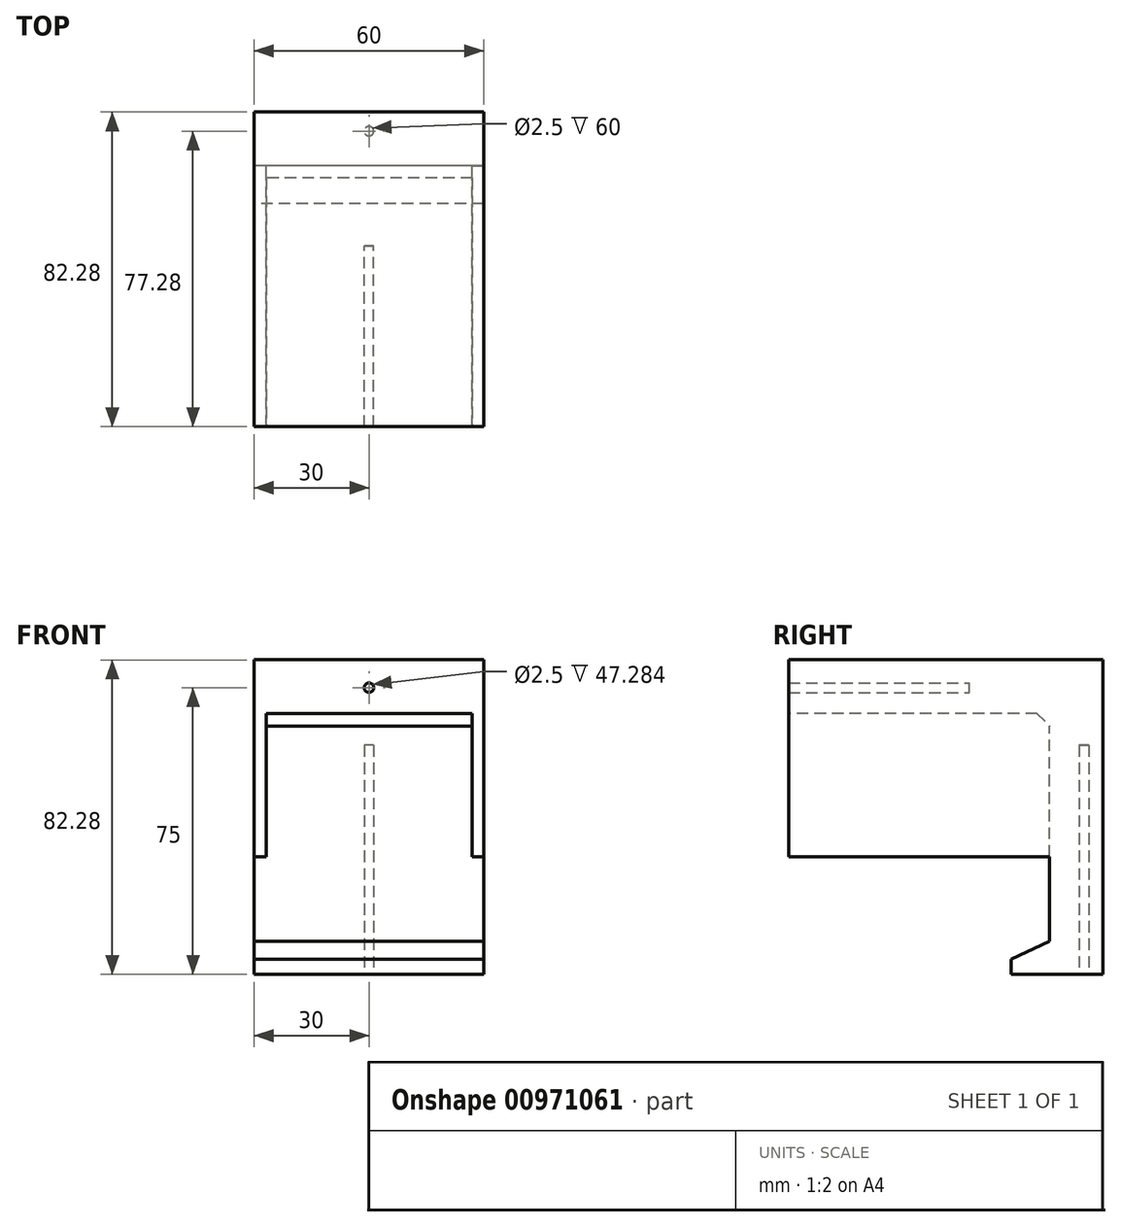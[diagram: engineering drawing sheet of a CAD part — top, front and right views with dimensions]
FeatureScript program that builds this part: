
annotation { "Feature Type Name" : "Feature", "Feature Type Description" : "" }
export const myFeature = defineFeature(function(context is Context, id is Id, definition is map)
    precondition{}
    {
        {
            var Q0;
            Q0=qCreatedBy(makeId("Right.planeOp"),FACE);
            var sketch = newSketch(context, id + "F0", { "sketchPlane" : qUnion([Q0])});
            skLineSegment(sketch, "E0", {"start": v(0, 0) * mm, "end": v(-4, 0) * mm});
            skLineSegment(sketch, "E1", {"start": v(-4, 0) * mm, "end": v(-4, 40) * mm});
            skLineSegment(sketch, "E2", {"start": v(-32.28, 68.28) * mm, "end": v(-72.28, 68.28) * mm});
            skLineSegment(sketch, "E3", {"start": v(-72.28, 68.28) * mm, "end": v(-72.28, 72.28) * mm});
            skLineSegment(sketch, "E4", {"start": v(-72.28, 72.28) * mm, "end": v(-72.28, 82.28) * mm});
            skLineSegment(sketch, "E5", {"start": v(-72.28, 82.28) * mm, "end": v(-68.28, 82.28) * mm});
            skLineSegment(sketch, "E6", {"start": v(-4, 0) * mm, "end": v(-14, 0) * mm});
            skLineSegment(sketch, "E7", {"start": v(0, 0) * mm, "end": v(10, 0) * mm});
            skLineSegment(sketch, "E8", {"start": v(-14, 0) * mm, "end": v(-14, 4) * mm});
            skLineSegment(sketch, "E9", {"start": v(10, 0) * mm, "end": v(10, 4) * mm});
            skLineSegment(sketch, "E10", {"start": v(-14, 4) * mm, "end": v(-4, 8.64) * mm});
            skLineSegment(sketch, "E11", {"start": v(-68.28, 82.28) * mm, "end": v(10, 82.28) * mm});
            skLineSegment(sketch, "E12", {"start": v(10, 82.28) * mm, "end": v(10, 4) * mm});
            skLineSegment(sketch, "E13", {"start": v(-32.28, 68.28) * mm, "end": v(-7.28, 68.28) * mm});
            skLineSegment(sketch, "E14", {"start": v(-4, 40) * mm, "end": v(-4, 65) * mm});
            skLineSegment(sketch, "E15", {"start": v(-7.28, 68.28) * mm, "end": v(-4, 65) * mm});
            skSolve(sketch);
        }
        {
            var Q0;
            Q0 = qSketchRegion(id + "F0", true);
            extrude(context, id + "F1", {"entities" : qUnion([Q0]), "depth" : 60 * mm, "offsetDistance" : 25 * mm});
        }
        {
            var Q0;
            Q0=qCreatedBy(makeId("Right.planeOp"),FACE);
            var sketch = newSketch(context, id + "F2", { "sketchPlane" : qUnion([Q0])});
            skLineSegment(sketch, "E16", {"start": v(-72.28, 70.85) * mm, "end": v(-72.28, 30.85) * mm});
            skLineSegment(sketch, "E17", {"start": v(-72.28, 30.85) * mm, "end": v(-2.28, 30.85) * mm});
            skLineSegment(sketch, "E18", {"start": v(-2.28, 30.85) * mm, "end": v(-2.28, 42.85) * mm});
            skLineSegment(sketch, "E19", {"start": v(-72.28, 70.85) * mm, "end": v(-30.52, 70.85) * mm});
            skLineSegment(sketch, "E20", {"start": v(-30.52, 70.85) * mm, "end": v(-2.47, 70.85) * mm});
            skLineSegment(sketch, "E21", {"start": v(-2.47, 70.85) * mm, "end": v(-2.28, 42.85) * mm});
            skSolve(sketch);
        }
        {
            var Q0;
            Q0 = qSketchRegion(id + "F2", true);
            extrude(context, id + "F3", {"entities" : qUnion([Q0]), "operationType" : NewBodyOperationType.ADD, "depth" : 3.1 * mm, "offsetDistance" : 25 * mm});
        }
        {
            var Q0;
            Q0=qCreatedBy(makeId("Right.planeOp"),FACE);
            cPlane(context, id + "F4", {"entities" : qUnion([Q0]), "cplaneType" : CPlaneType.OFFSET, "offset" : 60 * mm, "width" : 150 * mm, "height" : 150 * mm});
        }
        {
            var Q0;
            Q0=qCreatedBy(id+"F4.planeOp",FACE);
            var sketch = newSketch(context, id + "F5", { "sketchPlane" : qUnion([Q0])});
            skLineSegment(sketch, "E22", {"start": v(-72.28, 70.85) * mm, "end": v(-72.28, 30.85) * mm});
            skLineSegment(sketch, "E23", {"start": v(-72.28, 30.85) * mm, "end": v(-2.28, 30.85) * mm});
            skLineSegment(sketch, "E24", {"start": v(-2.28, 30.85) * mm, "end": v(-2.28, 42.85) * mm});
            skLineSegment(sketch, "E25", {"start": v(-72.28, 70.85) * mm, "end": v(-30.52, 70.85) * mm});
            skLineSegment(sketch, "E26", {"start": v(-2.28, 42.85) * mm, "end": v(-2.28, 70.85) * mm});
            skLineSegment(sketch, "E27", {"start": v(-2.28, 70.85) * mm, "end": v(-30.52, 70.85) * mm});
            skSolve(sketch);
        }
        {
            var Q0;
            Q0 = qSketchRegion(id + "F5", true);
            extrude(context, id + "F6", {"entities" : qUnion([Q0]), "operationType" : NewBodyOperationType.ADD, "oppositeDirection" : true, "depth" : 3 * mm, "offsetDistance" : 25 * mm});
        }
        {
            var Q0;
            Q0=qCreatedBy(makeId("Front.planeOp"),FACE);
            cPlane(context, id + "F7", {"entities" : qUnion([Q0]), "cplaneType" : CPlaneType.OFFSET, "offset" : 25 * mm, "width" : 150 * mm, "height" : 150 * mm});
        }
        {
            var Q0;
            Q0=qCreatedBy(id+"F7.planeOp",FACE);
            var sketch = newSketch(context, id + "F8", { "sketchPlane" : qUnion([Q0])});
            skCircle(sketch, "E28", {"center": v(30, 75) * mm, "radius": 1.25 * mm});
            skSolve(sketch);
        }
        {
            var Q0;
            Q0 = qSketchRegion(id + "F8", true);
            extrude(context, id + "F9", {"entities" : qUnion([Q0]), "operationType" : NewBodyOperationType.REMOVE, "depth" : 100 * mm, "offsetDistance" : 25 * mm});
        }
        {
            var Q0;
            Q0=qCreatedBy(makeId("Top.planeOp"),FACE);
            var sketch = newSketch(context, id + "F10", { "sketchPlane" : qUnion([Q0])});
            skCircle(sketch, "E29", {"center": v(30, 5) * mm, "radius": 1.25 * mm});
            skSolve(sketch);
        }
        {
            var Q0;
            Q0 = qSketchRegion(id + "F10", true);
            extrude(context, id + "F11", {"entities" : qUnion([Q0]), "operationType" : NewBodyOperationType.REMOVE, "depth" : 60 * mm, "offsetDistance" : 25 * mm});
        }
    });
